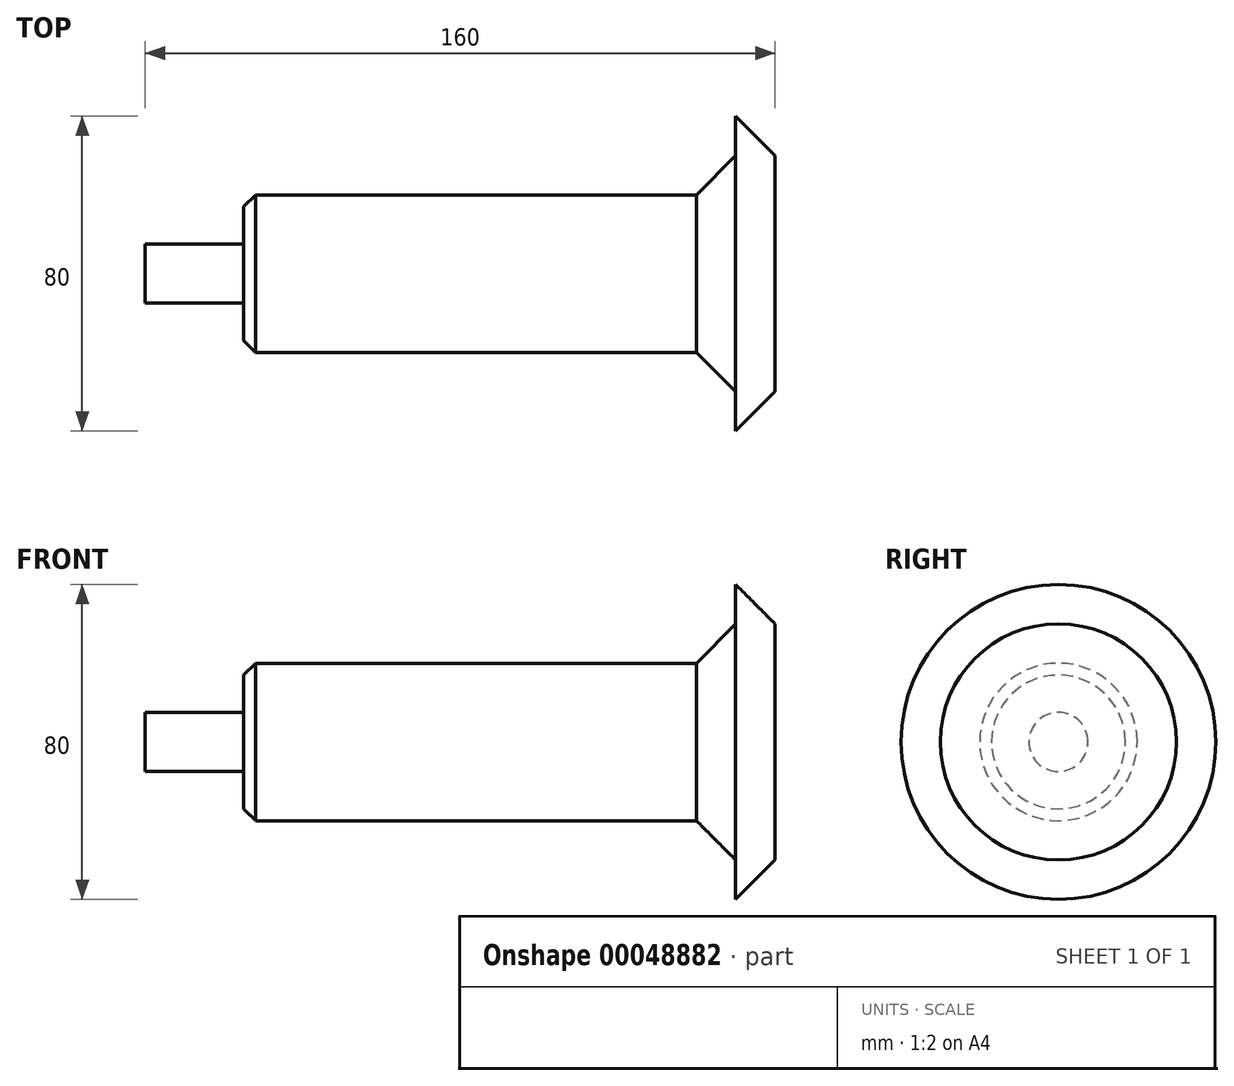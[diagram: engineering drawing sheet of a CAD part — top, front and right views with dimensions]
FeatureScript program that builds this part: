
annotation { "Feature Type Name" : "Feature", "Feature Type Description" : "" }
export const myFeature = defineFeature(function(context is Context, id is Id, definition is map)
    precondition{}
    {
        {
            var Q0;
            Q0=qCreatedBy(makeId("Front.planeOp"),FACE);
            var sketch = newSketch(context, id + "F0", { "sketchPlane" : qUnion([Q0])});
            skLineSegment(sketch, "E0", {"start": v(0, 0) * mm, "end": v(0, 7.5) * mm});
            skLineSegment(sketch, "E1", {"start": v(0, 7.5) * mm, "end": v(25, 7.5) * mm});
            skLineSegment(sketch, "E2", {"start": v(25, 7.5) * mm, "end": v(25, 20) * mm});
            skLineSegment(sketch, "E3", {"start": v(25, 20) * mm, "end": v(150, 20) * mm});
            skLineSegment(sketch, "E4", {"start": v(140, 30) * mm, "end": v(140, 30) * mm});
            skLineSegment(sketch, "E5", {"start": v(150, 40) * mm, "end": v(160, 40) * mm});
            skLineSegment(sketch, "E6", {"start": v(160, 40) * mm, "end": v(160, 0) * mm});
            skLineSegment(sketch, "E7", {"start": v(160, 0) * mm, "end": v(0, 0) * mm});
            skLineSegment(sketch, "E8", {"start": v(150, 20) * mm, "end": v(150, 40) * mm});
            skSolve(sketch);
        }
        {
            var Q0;
            Q0=makeQuery(id+"F0.imprint","IMPRINT",FACE,{"disambiguationData":[TD([[makeQuery(id+"F0.imprint","IMPRINT",EDGE,{"derivedFrom":sQuery(id+"F0.wireOp",EDGE,"E0")}),-1.0]])]});
            var Q1;
            Q1=sQuery(id+"F0.wireOp",EDGE,"E7");
            revolve(context, id + "F1", {"entities" : qUnion([Q0]), "axis" : qUnion([Q1]), "revolveType" : RevolveType.FULL});
        }
        {
            var Q0;
            Q0=makeQuery(id+"F1.opRevolve","SWEPT_EDGE",EDGE,{"disambiguationData":[OSD([sQuery(id+"F0.wireOp",EDGE,"E2"),sQuery(id+"F0.wireOp",EDGE,"E3")])]});
            chamfer(context, id + "F2", {"entities" : qUnion([Q0]), "chamferType" : ChamferType.OFFSET_ANGLE, "width" : 3 * mm, "oppositeDirection" : false, "angle" : 45 * degree, "tangentPropagation" : true});
        }
        {
            var Q0;
            Q0=makeQuery(id+"F1.opRevolve","SWEPT_EDGE",EDGE,{"disambiguationData":[OSD([sQuery(id+"F0.wireOp",EDGE,"E3"),sQuery(id+"F0.wireOp",EDGE,"E8")])]});
            chamfer(context, id + "F3", {"entities" : qUnion([Q0]), "chamferType" : ChamferType.OFFSET_ANGLE, "width" : 10 * mm, "oppositeDirection" : false, "angle" : 45 * degree, "tangentPropagation" : true});
        }
        {
            var Q0;
            Q0=makeQuery(id+"F1.opRevolve","SWEPT_EDGE",EDGE,{"disambiguationData":[OSD([sQuery(id+"F0.wireOp",EDGE,"E5"),sQuery(id+"F0.wireOp",EDGE,"E6")])]});
            chamfer(context, id + "F4", {"entities" : qUnion([Q0]), "chamferType" : ChamferType.OFFSET_ANGLE, "width" : 10 * mm, "oppositeDirection" : false, "angle" : 45 * degree, "tangentPropagation" : true});
        }
    });
